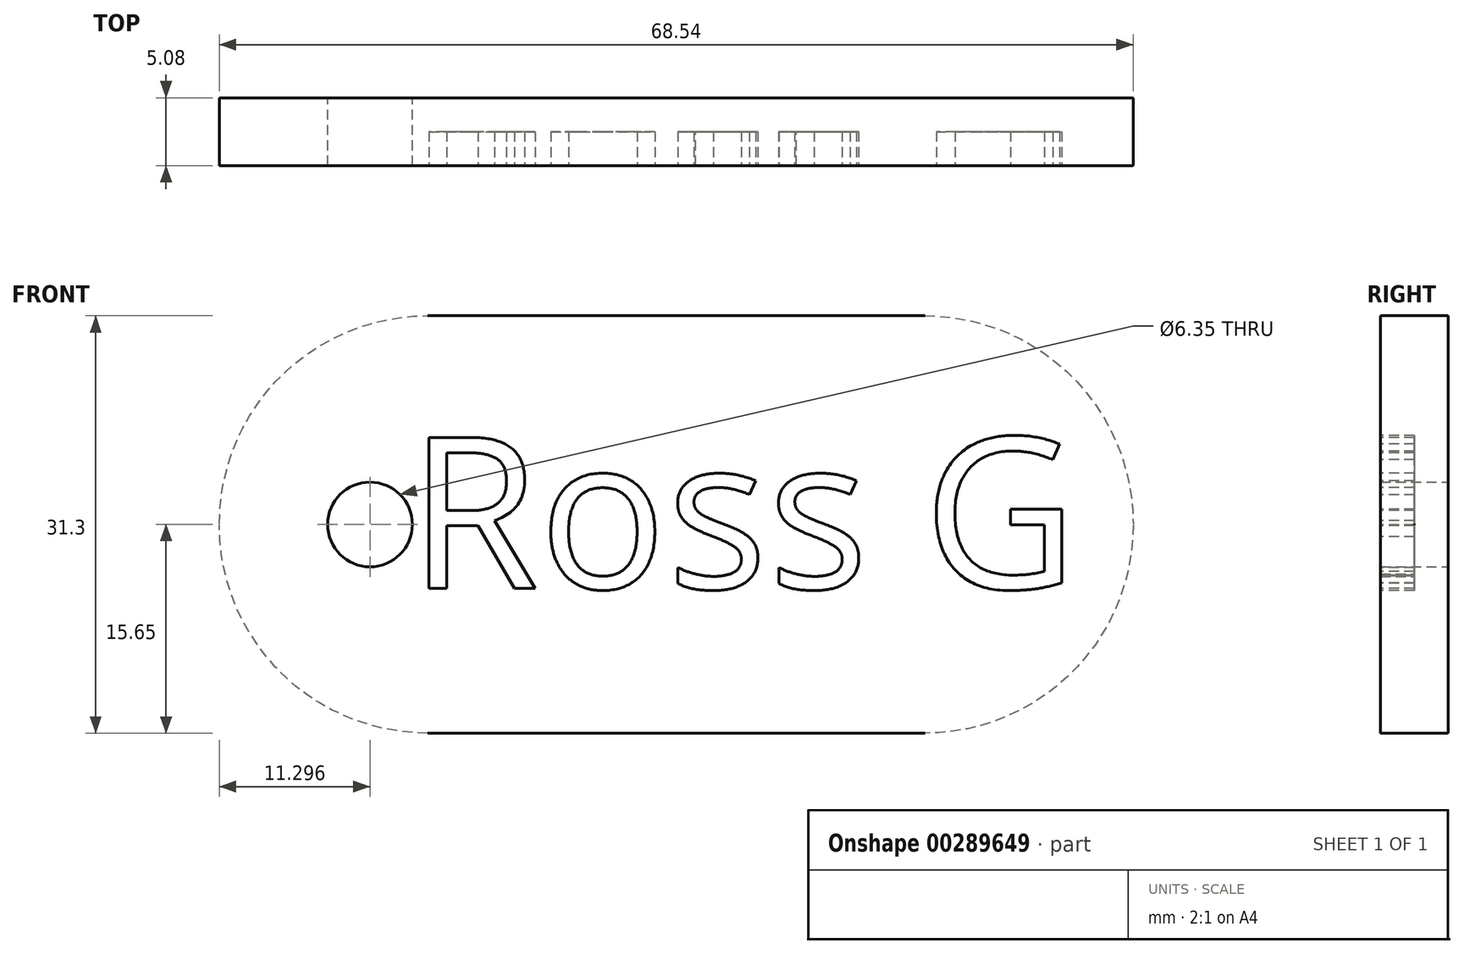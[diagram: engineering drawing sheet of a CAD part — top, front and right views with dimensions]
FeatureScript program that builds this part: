
annotation { "Feature Type Name" : "Feature", "Feature Type Description" : "" }
export const myFeature = defineFeature(function(context is Context, id is Id, definition is map)
    precondition{}
    {
        {
            var Q0;
            Q0=qCreatedBy(makeId("Front.planeOp"),FACE);
            var sketch = newSketch(context, id + "F0", { "sketchPlane" : qUnion([Q0])});
            skLineSegment(sketch, "E0.bottom", {"start": v(18.65, 15.65) * mm, "end": v(-18.65, 15.65) * mm});
            skLineSegment(sketch, "E0.top", {"start": v(18.65, -15.65) * mm, "end": v(-18.65, -15.65) * mm});
            skLineSegment(sketch, "E0.left", {"start": v(34.27, 0.03) * mm, "end": v(34.27, -0.03) * mm});
            skLineSegment(sketch, "E0.right", {"start": v(-34.27, 0.03) * mm, "end": v(-34.27, -0.03) * mm});
            skPoint(sketch, "E0.middle", {"position": v(0, 0) * mm});
            skPoint(sketch, "E1.visualSharp", {"position": v(-34.27, 15.65) * mm});
            skArc(sketch, "E1.filletArc", {"start": v(-18.65, 15.65) * mm, "mid": v(-29.7, 11.07) * mm, "end": v(-34.27, 0.03) * mm});
            skPoint(sketch, "E2.visualSharp", {"position": v(-34.27, -15.65) * mm});
            skArc(sketch, "E2.filletArc", {"start": v(-34.27, -0.03) * mm, "mid": v(-29.7, -11.07) * mm, "end": v(-18.65, -15.65) * mm});
            skPoint(sketch, "E3.visualSharp", {"position": v(34.27, -15.65) * mm});
            skArc(sketch, "E3.filletArc", {"start": v(18.65, -15.65) * mm, "mid": v(29.7, -11.07) * mm, "end": v(34.27, -0.03) * mm});
            skPoint(sketch, "E4.visualSharp", {"position": v(34.27, 15.65) * mm});
            skArc(sketch, "E4.filletArc", {"start": v(34.27, 0.03) * mm, "mid": v(29.7, 11.07) * mm, "end": v(18.65, 15.65) * mm});
            skSolve(sketch);
        }
        {
            var Q0;
            Q0=makeQuery(id+"F0.imprint","IMPRINT",FACE,{"disambiguationData":[TD([[makeQuery(id+"F0.imprint","IMPRINT",EDGE,{"derivedFrom":sQuery(id+"F0.wireOp",EDGE,"E0.bottom")}),1.0]])]});
            var Q1;
            Q1=sQuery(id+"F0.wireOp",EDGE,"E0.right");
            var Q2;
            Q2=sQuery(id+"F0.wireOp",EDGE,"E0.left");
            var Q3;
            Q3=sQuery(id+"F0.wireOp",EDGE,"E0.bottom");
            var Q4;
            Q4=sQuery(id+"F0.wireOp",EDGE,"E0.top");
            extrude(context, id + "F1", {"entities" : qUnion([Q0]), "surfaceEntities" : qUnion([Q1, Q2, Q3, Q4]), "depth" : 5.08 * mm});
        }
        {
            var Q0;
            Q0=makeQuery(id+"F1.opExtrude","SWEPT_FACE",FACE,{"disambiguationData":[OSD([sQuery(id+"F0.wireOp",EDGE,"E0.left")])]});
            var Q1;
            Q1=makeQuery(id+"F1.opExtrude","SWEPT_FACE",FACE,{"disambiguationData":[OSD([sQuery(id+"F0.wireOp",EDGE,"E0.right")])]});
            fillet(context, id + "F2", {"entities" : qUnion([Q0, Q1]), "radius" : 2.54 * mm, "tangentPropagation" : true, "rho" : .99, "crossSection" : FilletCrossSection.CONIC, "allowEdgeOverflow" : false});
        }
        {
            var Q0;
            Q0=qCreatedBy(makeId("Front.planeOp"),FACE);
            var sketch = newSketch(context, id + "F3", { "sketchPlane" : qUnion([Q0])});
            skCircle(sketch, "E5", {"center": v(-22.97, 0) * mm, "radius": 3.17 * mm});
            skSolve(sketch);
        }
        {
            var Q0;
            Q0 = qSketchRegion(id + "F3", true);
            extrude(context, id + "F4", {"entities" : qUnion([Q0]), "operationType" : NewBodyOperationType.REMOVE, "depth" : 5.08 * mm});
        }
        {
            var Q0;
            Q0=makeQuery(id+"F1.opExtrude","CAP_FACE",FACE,{"disambiguationData":[OSD([sQuery(id+"F0.wireOp",EDGE,"E0.bottom"),sQuery(id+"F0.wireOp",EDGE,"E0.top"),sQuery(id+"F0.wireOp",EDGE,"E0.left"),sQuery(id+"F0.wireOp",EDGE,"E0.right"),sQuery(id+"F0.wireOp",EDGE,"E1.filletArc"),sQuery(id+"F0.wireOp",EDGE,"E2.filletArc"),sQuery(id+"F0.wireOp",EDGE,"E3.filletArc"),sQuery(id+"F0.wireOp",EDGE,"E4.filletArc")])],"isStart":false});
            var sketch = newSketch(context, id + "F5", { "sketchPlane" : qUnion([Q0])});
            skText(sketch, "E6", { "text": "Ross G", "fontName": "OpenSans-Regular.ttf"});
            const initialGuessF5  = {"E6": [-0.0201, -0.0048, 1, 0, 0.01142]};
            skSetInitialGuess(sketch, initialGuessF5);
            skSolve(sketch);
        }
        {
            var Q0;
            Q0 = qSketchRegion(id + "F5", true);
            extrude(context, id + "F6", {"entities" : qUnion([Q0]), "operationType" : NewBodyOperationType.REMOVE, "oppositeDirection" : true, "depth" : 2.54 * mm});
        }
    });
